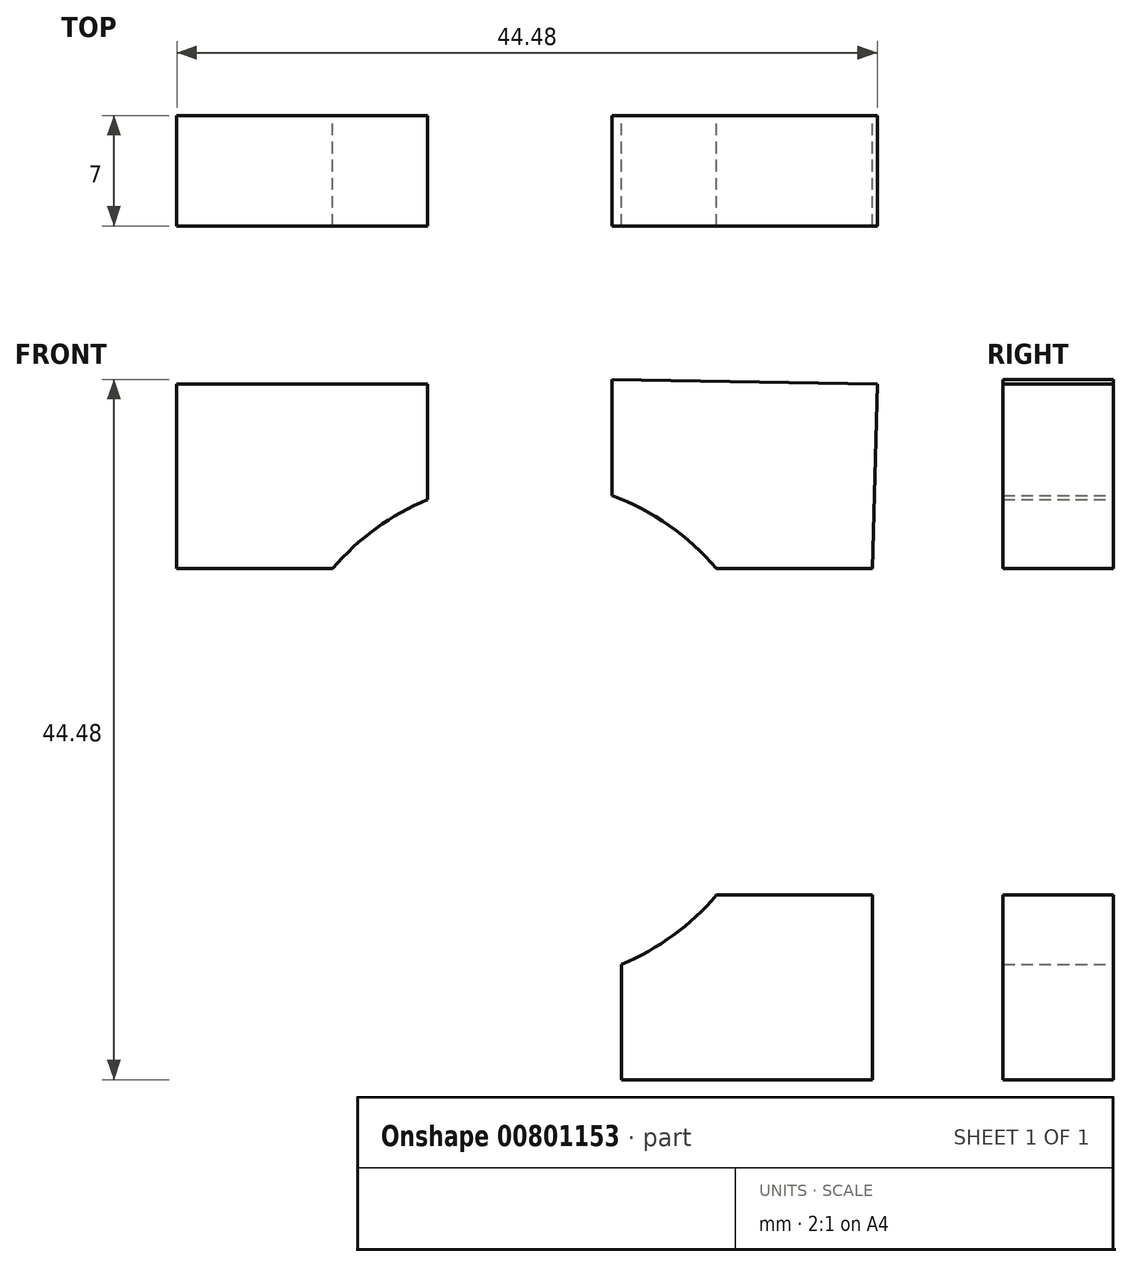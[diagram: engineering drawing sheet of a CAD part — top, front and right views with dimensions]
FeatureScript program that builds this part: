
annotation { "Feature Type Name" : "Feature", "Feature Type Description" : "" }
export const myFeature = defineFeature(function(context is Context, id is Id, definition is map)
    precondition{}
    {
        {
            var Q0;
            Q0=qCreatedBy(makeId("Front.planeOp"),FACE);
            var sketch = newSketch(context, id + "F0", { "sketchPlane" : qUnion([Q0])});
            skCircle(sketch, "E0", {"center": v(0, 0) * mm, "radius": 16 * mm});
            skLineSegment(sketch, "E1.top", {"start": v(-22.1, -22.4) * mm, "end": v(22.4, -22.4) * mm});
            skLineSegment(sketch, "E2.bottom", {"start": v(-22.1, 10.37) * mm, "end": v(-6.16, 10.37) * mm});
            skLineSegment(sketch, "E2.top", {"start": v(-22.1, 22.1) * mm, "end": v(-6.16, 22.1) * mm});
            skLineSegment(sketch, "E2.left", {"start": v(-22.1, 10.37) * mm, "end": v(-22.1, 22.1) * mm});
            skLineSegment(sketch, "E2.right", {"start": v(-6.16, 10.37) * mm, "end": v(-6.16, 22.1) * mm});
            skLineSegment(sketch, "E3.1.0", {"start": v(22.1, -10.37) * mm, "end": v(22.1, -22.1) * mm});
            skLineSegment(sketch, "E3.1.1", {"start": v(22.1, -10.37) * mm, "end": v(6.16, -10.37) * mm});
            skLineSegment(sketch, "E3.1.2", {"start": v(6.16, -10.37) * mm, "end": v(6.16, -22.1) * mm});
            skLineSegment(sketch, "E3.1.3", {"start": v(22.1, -22.1) * mm, "end": v(6.16, -22.1) * mm});
            skLineSegment(sketch, "E4.bottom", {"start": v(-22.1, -10.37) * mm, "end": v(-5.56, -10.37) * mm});
            skLineSegment(sketch, "E4.top", {"start": v(-22.1, -22.4) * mm, "end": v(-5.56, -22.4) * mm});
            skLineSegment(sketch, "E4.left", {"start": v(-22.1, -10.37) * mm, "end": v(-22.1, -22.4) * mm});
            skLineSegment(sketch, "E4.right", {"start": v(-5.56, -10.37) * mm, "end": v(-5.56, -22.4) * mm});
            skLineSegment(sketch, "E5.1.0", {"start": v(22.1, 10.37) * mm, "end": v(5.56, 10.37) * mm});
            skLineSegment(sketch, "E5.1.1", {"start": v(5.56, 10.37) * mm, "end": v(5.56, 22.4) * mm});
            skLineSegment(sketch, "E5.1.2", {"start": v(22.1, 22.4) * mm, "end": v(5.56, 22.4) * mm});
            skLineSegment(sketch, "E6", {"start": v(22.4, 22.1) * mm, "end": v(22.1, 10.37) * mm});
            skLineSegment(sketch, "E7", {"start": v(22.4, 22.1) * mm, "end": v(5.56, 22.4) * mm});
            skSolve(sketch);
        }
        {
            var Q0;
            {var subQ1=sQuery(id+"F0.wireOp",EDGE,"E2.top");Q0=makeQuery(id+"F0.imprint","IMPRINT",FACE,{"disambiguationData":[TD([[makeQuery(id+"F0.imprint","IMPRINT",EDGE,{"derivedFrom":subQ1}),-1.0]])]});}
            var Q1;
            {var subQ4=sQuery(id+"F0.wireOp",EDGE,"E6");Q1=makeQuery(id+"F0.imprint","IMPRINT",FACE,{"disambiguationData":[TD([[makeQuery(id+"F0.imprint","IMPRINT",EDGE,{"derivedFrom":subQ4}),-1.0]])]});}
            var Q2;
            {var subQ1=sQuery(id+"F0.wireOp",EDGE,"E4.top");Q2=makeQuery(id+"F0.imprint","IMPRINT",FACE,{"disambiguationData":[TD([[makeQuery(id+"F0.imprint","IMPRINT",EDGE,{"derivedFrom":subQ1}),1.0]])]});}
            var Q3;
            {var subQ5=sQuery(id+"F0.wireOp",EDGE,"E3.1.0");Q3=makeQuery(id+"F0.imprint","IMPRINT",FACE,{"disambiguationData":[TD([[makeQuery(id+"F0.imprint","IMPRINT",EDGE,{"derivedFrom":subQ5}),-1.0]])]});}
            extrude(context, id + "F1", {"entities" : qUnion([Q0, Q1, Q2, Q3]), "depth" : 7 * mm, "offsetDistance" : 25 * mm});
        }
    });
